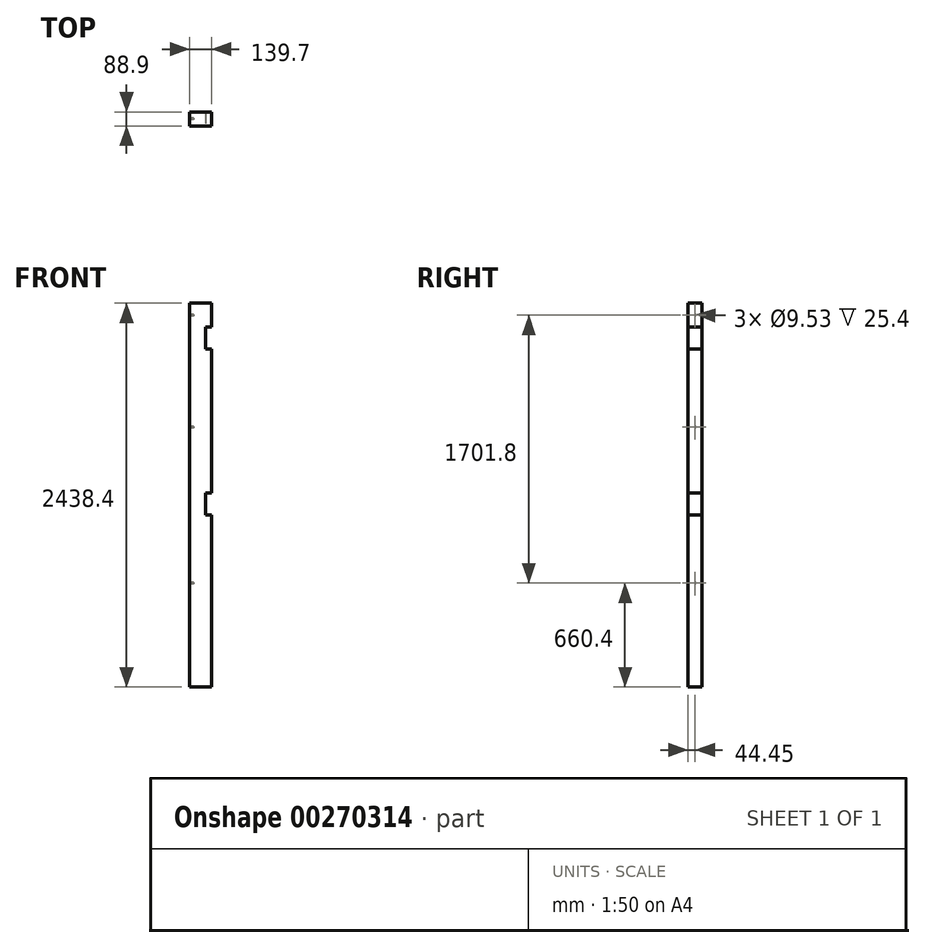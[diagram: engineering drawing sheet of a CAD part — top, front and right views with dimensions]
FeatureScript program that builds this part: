
annotation { "Feature Type Name" : "Feature", "Feature Type Description" : "" }
export const myFeature = defineFeature(function(context is Context, id is Id, definition is map)
    precondition{}
    {
        {
            var Q0;
            Q0=qCreatedBy(makeId("Top.planeOp"),FACE);
            var sketch = newSketch(context, id + "F0", { "sketchPlane" : qUnion([Q0])});
            skLineSegment(sketch, "E0.bottom", {"start": v(69.85, -44.45) * mm, "end": v(-69.85, -44.45) * mm});
            skLineSegment(sketch, "E0.top", {"start": v(69.85, 44.45) * mm, "end": v(-69.85, 44.45) * mm});
            skLineSegment(sketch, "E0.left", {"start": v(69.85, -44.45) * mm, "end": v(69.85, 44.45) * mm});
            skLineSegment(sketch, "E0.right", {"start": v(-69.85, -44.45) * mm, "end": v(-69.85, 44.45) * mm});
            skPoint(sketch, "E0.middle", {"position": v(0, 0) * mm});
            skSolve(sketch);
        }
        {
            var Q0;
            Q0=makeQuery(id+"F0.imprint","IMPRINT",FACE,{"disambiguationData":[TD([[makeQuery(id+"F0.imprint","IMPRINT",EDGE,{"derivedFrom":sQuery(id+"F0.wireOp",EDGE,"E0.bottom")}),-1.0]])]});
            extrude(context, id + "F1", {"entities" : qUnion([Q0]), "endBound" : BoundingType.SYMMETRIC, "depth" : 2438.4 * mm});
        }
        {
            var Q0;
            Q0=makeQuery(id+"F1.opExtrude","SWEPT_FACE",FACE,{"disambiguationData":[OSD([sQuery(id+"F0.wireOp",EDGE,"E0.left")])]});
            var sketch = newSketch(context, id + "F2", { "sketchPlane" : qUnion([Q0])});
            skLineSegment(sketch, "E1.bottom", {"start": v(44.45, 927.1) * mm, "end": v(-44.45, 927.1) * mm});
            skLineSegment(sketch, "E1.top", {"start": v(44.45, 1066.8) * mm, "end": v(-44.45, 1066.8) * mm});
            skLineSegment(sketch, "E1.left", {"start": v(44.45, 927.1) * mm, "end": v(44.45, 1066.8) * mm});
            skLineSegment(sketch, "E1.right", {"start": v(-44.45, 927.1) * mm, "end": v(-44.45, 1066.8) * mm});
            skPoint(sketch, "E1.middle", {"position": v(0, 996.95) * mm});
            skLineSegment(sketch, "E2.bottom", {"start": v(44.45, -127) * mm, "end": v(-44.45, -127) * mm});
            skLineSegment(sketch, "E2.top", {"start": v(44.45, 12.7) * mm, "end": v(-44.45, 12.7) * mm});
            skLineSegment(sketch, "E2.left", {"start": v(44.45, -127) * mm, "end": v(44.45, 12.7) * mm});
            skLineSegment(sketch, "E2.right", {"start": v(-44.45, -127) * mm, "end": v(-44.45, 12.7) * mm});
            skPoint(sketch, "E2.middle", {"position": v(0, -57.15) * mm});
            skSolve(sketch);
        }
        {
            var Q0;
            Q0 = qSketchRegion(id + "F2", true);
            extrude(context, id + "F3", {"entities" : qUnion([Q0]), "operationType" : NewBodyOperationType.REMOVE, "oppositeDirection" : true, "depth" : 38.1 * mm});
        }
        {
            var Q0;
            Q0=makeQuery(id+"F1.opExtrude","SWEPT_FACE",FACE,{"disambiguationData":[OSD([sQuery(id+"F0.wireOp",EDGE,"E0.right")])]});
            var sketch = newSketch(context, id + "F4", { "sketchPlane" : qUnion([Q0])});
            skCircle(sketch, "E3", {"center": v(0, -558.8) * mm, "radius": 4.76 * mm});
            skPoint(sketch, "E3.centerSnap0", {"position": v(0, -1219.2) * mm});
            skCircle(sketch, "E4", {"center": v(0, 431.8) * mm, "radius": 4.76 * mm});
            skCircle(sketch, "E5", {"center": v(0, 1143) * mm, "radius": 4.76 * mm});
            skSolve(sketch);
        }
        {
            var Q0;
            Q0 = qSketchRegion(id + "F4", true);
            extrude(context, id + "F5", {"entities" : qUnion([Q0]), "operationType" : NewBodyOperationType.REMOVE, "oppositeDirection" : true, "depth" : 25.4 * mm});
        }
    });
